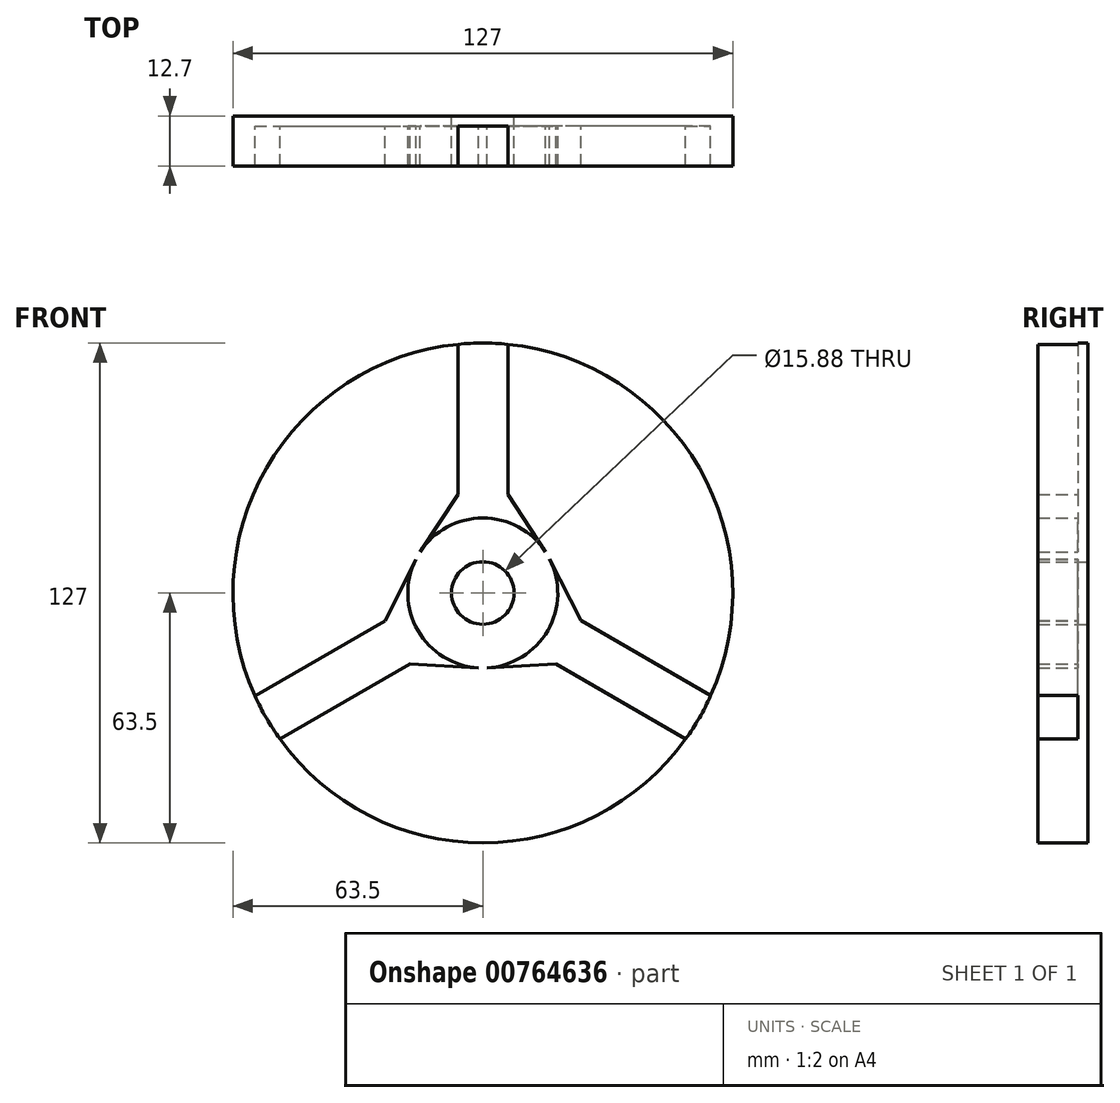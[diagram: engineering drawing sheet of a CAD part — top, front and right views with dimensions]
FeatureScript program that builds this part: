
annotation { "Feature Type Name" : "Feature", "Feature Type Description" : "" }
export const myFeature = defineFeature(function(context is Context, id is Id, definition is map)
    precondition{}
    {
        {
            var Q0;
            Q0=qCreatedBy(makeId("Front.planeOp"),FACE);
            var sketch = newSketch(context, id + "F0", { "sketchPlane" : qUnion([Q0])});
            skCircle(sketch, "E0", {"center": v(0, 0) * mm, "radius": 63.5 * mm});
            skLineSegment(sketch, "E1", {"start": v(0, 63.5) * mm, "end": v(0, 0) * mm, "construction": true});
            skLineSegment(sketch, "E2", {"start": v(0, 0) * mm, "end": v(55, -31.75) * mm, "construction": true});
            skLineSegment(sketch, "E3", {"start": v(0, 0) * mm, "end": v(-55, -31.75) * mm, "construction": true});
            skLineSegment(sketch, "E4", {"start": v(57.9, -26.08) * mm, "end": v(24.9, -7.03) * mm});
            skLineSegment(sketch, "E5", {"start": v(51.55, -37.08) * mm, "end": v(18.55, -18.03) * mm});
            skLineSegment(sketch, "E6", {"start": v(-57.89, -26.1) * mm, "end": v(-24.9, -7.05) * mm});
            skLineSegment(sketch, "E7", {"start": v(-51.54, -37.1) * mm, "end": v(-18.54, -18.05) * mm});
            skLineSegment(sketch, "E8", {"start": v(6.35, 63.18) * mm, "end": v(6.35, 25.08) * mm});
            skLineSegment(sketch, "E9", {"start": v(-6.35, 63.18) * mm, "end": v(-6.35, 25.08) * mm});
            skLineSegment(sketch, "E10", {"start": v(24.9, -7.03) * mm, "end": v(18.55, -18.03) * mm, "construction": true});
            skLineSegment(sketch, "E11", {"start": v(-24.9, -7.05) * mm, "end": v(-18.54, -18.05) * mm, "construction": true});
            skLineSegment(sketch, "E12", {"start": v(-6.35, 25.08) * mm, "end": v(6.35, 25.08) * mm, "construction": true});
            skLineSegment(sketch, "E13", {"start": v(-18.54, -18.05) * mm, "end": v(-1.06, -19.02) * mm});
            skLineSegment(sketch, "E14", {"start": v(18.55, -18.03) * mm, "end": v(1.07, -19.02) * mm});
            skLineSegment(sketch, "E15", {"start": v(-24.9, -7.05) * mm, "end": v(-17, 8.58) * mm});
            skLineSegment(sketch, "E16", {"start": v(-6.35, 25.08) * mm, "end": v(-15.94, 10.43) * mm});
            skLineSegment(sketch, "E17", {"start": v(6.35, 25.08) * mm, "end": v(15.94, 10.43) * mm});
            skLineSegment(sketch, "E18", {"start": v(24.9, -7.03) * mm, "end": v(17, 8.6) * mm});
            skLineSegment(sketch, "E19", {"start": v(-15.94, 10.43) * mm, "end": v(-15.94, 10.43) * mm});
            skArc(sketch, "E20", {"start": v(-1.06, -19.02) * mm, "mid": v(0, -19.05) * mm, "end": v(1.07, -19.02) * mm});
            skArc(sketch, "E21", {"start": v(1.07, -19.02) * mm, "mid": v(17, -8.58) * mm, "end": v(15.94, 10.43) * mm});
            skLineSegment(sketch, "E22", {"start": v(17, 8.6) * mm, "end": v(17, 8.6) * mm});
            skArc(sketch, "E23", {"start": v(15.94, 10.43) * mm, "mid": v(0, 19.05) * mm, "end": v(-15.94, 10.43) * mm});
            skArc(sketch, "E24", {"start": v(-15.94, 10.43) * mm, "mid": v(-16.5, 9.52) * mm, "end": v(-17, 8.58) * mm});
            skArc(sketch, "E25", {"start": v(-17, 8.58) * mm, "mid": v(-16.5, -9.53) * mm, "end": v(-1.06, -19.02) * mm});
            skCircle(sketch, "E26", {"center": v(0, 0) * mm, "radius": 7.94 * mm});
            skSolve(sketch);
        }
        {
            var Q0;
            {var subQ0=sQuery(id+"F0.wireOp",EDGE,"E6");Q0=makeQuery(id+"F0.imprint","IMPRINT",FACE,{"disambiguationData":[TD([[makeQuery(id+"F0.imprint","IMPRINT",EDGE,{"derivedFrom":subQ0}),1.0]])]});}
            var Q1;
            {var subQ1=sQuery(id+"F0.wireOp",EDGE,"E5");Q1=makeQuery(id+"F0.imprint","IMPRINT",FACE,{"disambiguationData":[TD([[makeQuery(id+"F0.imprint","IMPRINT",EDGE,{"derivedFrom":subQ1}),1.0]])]});}
            var Q2;
            {var subQ3=sQuery(id+"F0.wireOp",EDGE,"E20");Q2=makeQuery(id+"F0.imprint","IMPRINT",FACE,{"disambiguationData":[TD([[makeQuery(id+"F0.imprint","IMPRINT",EDGE,{"derivedFrom":subQ3}),1.0]])]});}
            var Q3;
            {var subQ1=sQuery(id+"F0.wireOp",EDGE,"E4");Q3=makeQuery(id+"F0.imprint","IMPRINT",FACE,{"disambiguationData":[TD([[makeQuery(id+"F0.imprint","IMPRINT",EDGE,{"derivedFrom":subQ1}),-1.0]])]});}
            extrude(context, id + "F1", {"entities" : qUnion([Q0, Q1, Q2, Q3]), "depth" : 12.7 * mm, "offsetDistance" : 25.4 * mm});
        }
        {
            var Q0;
            {var subQ1=sQuery(id+"F0.wireOp",EDGE,"E6");Q0=makeQuery(id+"F0.imprint","IMPRINT",FACE,{"disambiguationData":[TD([[makeQuery(id+"F0.imprint","IMPRINT",EDGE,{"derivedFrom":subQ1}),-1.0]])]});}
            var Q1;
            {var subQ2=sQuery(id+"F0.wireOp",EDGE,"E4");Q1=makeQuery(id+"F0.imprint","IMPRINT",FACE,{"disambiguationData":[TD([[makeQuery(id+"F0.imprint","IMPRINT",EDGE,{"derivedFrom":subQ2}),1.0]])]});}
            var Q2;
            {var subQ1=sQuery(id+"F0.wireOp",EDGE,"E8");Q2=makeQuery(id+"F0.imprint","IMPRINT",FACE,{"disambiguationData":[TD([[makeQuery(id+"F0.imprint","IMPRINT",EDGE,{"derivedFrom":subQ1}),-1.0]])]});}
            extrude(context, id + "F2", {"entities" : qUnion([Q0, Q1, Q2]), "operationType" : NewBodyOperationType.ADD, "depth" : 2.54 * mm, "offsetDistance" : 25.4 * mm});
        }
    });
